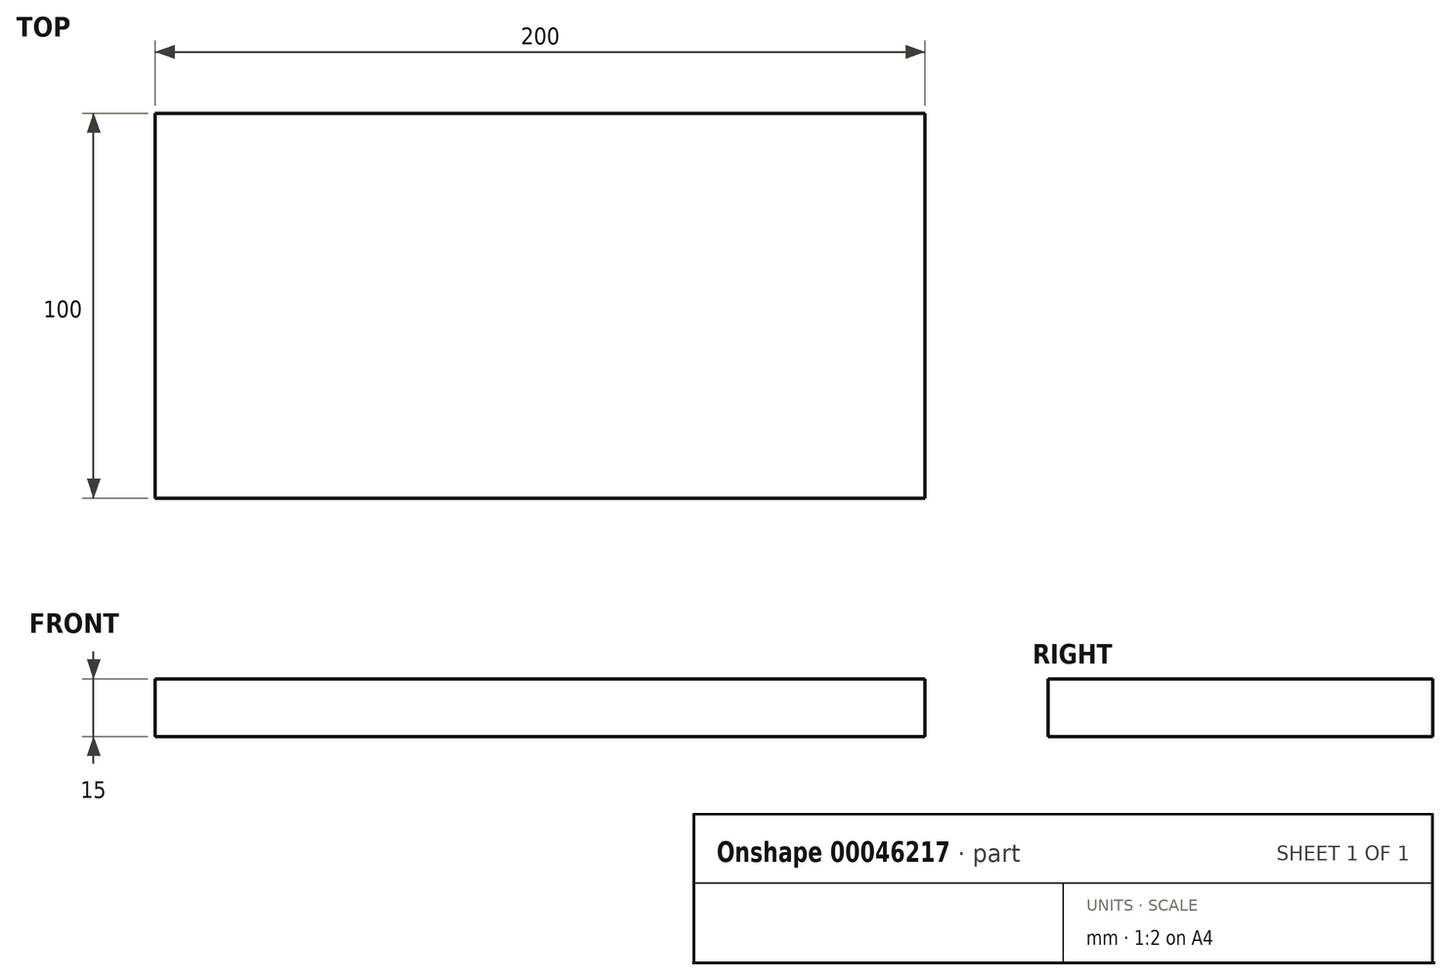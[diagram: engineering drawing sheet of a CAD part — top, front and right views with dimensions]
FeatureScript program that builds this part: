
annotation { "Feature Type Name" : "Feature", "Feature Type Description" : "" }
export const myFeature = defineFeature(function(context is Context, id is Id, definition is map)
    precondition{}
    {
        {
            var Q0;
            Q0=qCreatedBy(makeId("Top.planeOp"),FACE);
            var sketch = newSketch(context, id + "F0", { "sketchPlane" : qUnion([Q0])});
            skLineSegment(sketch, "E0.rect.bottom", {"start": v(-100, 50) * mm, "end": v(100, 50) * mm});
            skLineSegment(sketch, "E0.rect.top", {"start": v(-100, -50) * mm, "end": v(100, -50) * mm});
            skLineSegment(sketch, "E0.rect.left", {"start": v(-100, 50) * mm, "end": v(-100, -50) * mm});
            skLineSegment(sketch, "E0.rect.right", {"start": v(100, 50) * mm, "end": v(100, -50) * mm});
            skPoint(sketch, "E0.rect.middle", {"position": v(0, 0) * mm});
            skSolve(sketch);
        }
        {
            var Q0;
            Q0=makeQuery(id+"F0.imprint","IMPRINT",FACE,{"disambiguationData":[TD([[makeQuery(id+"F0.imprint","IMPRINT",EDGE,{"derivedFrom":sQuery(id+"F0.wireOp",EDGE,"E0.rect.bottom")}),-1.0]])]});
            extrude(context, id + "F1", {"entities" : qUnion([Q0]), "depth" : 15 * mm});
        }
        {
            var Q0;
            Q0=makeQuery(id+"F1.opExtrude","SWEPT_FACE",FACE,{"disambiguationData":[OSD([sQuery(id+"F0.wireOp",EDGE,"E0.rect.bottom")])]});
            cPlane(context, id + "F2", {"entities" : qUnion([Q0]), "cplaneType" : CPlaneType.OFFSET, "offset" : 15 * mm, "oppositeDirection" : true, "width" : 150 * mm, "height" : 150 * mm});
        }
    });
